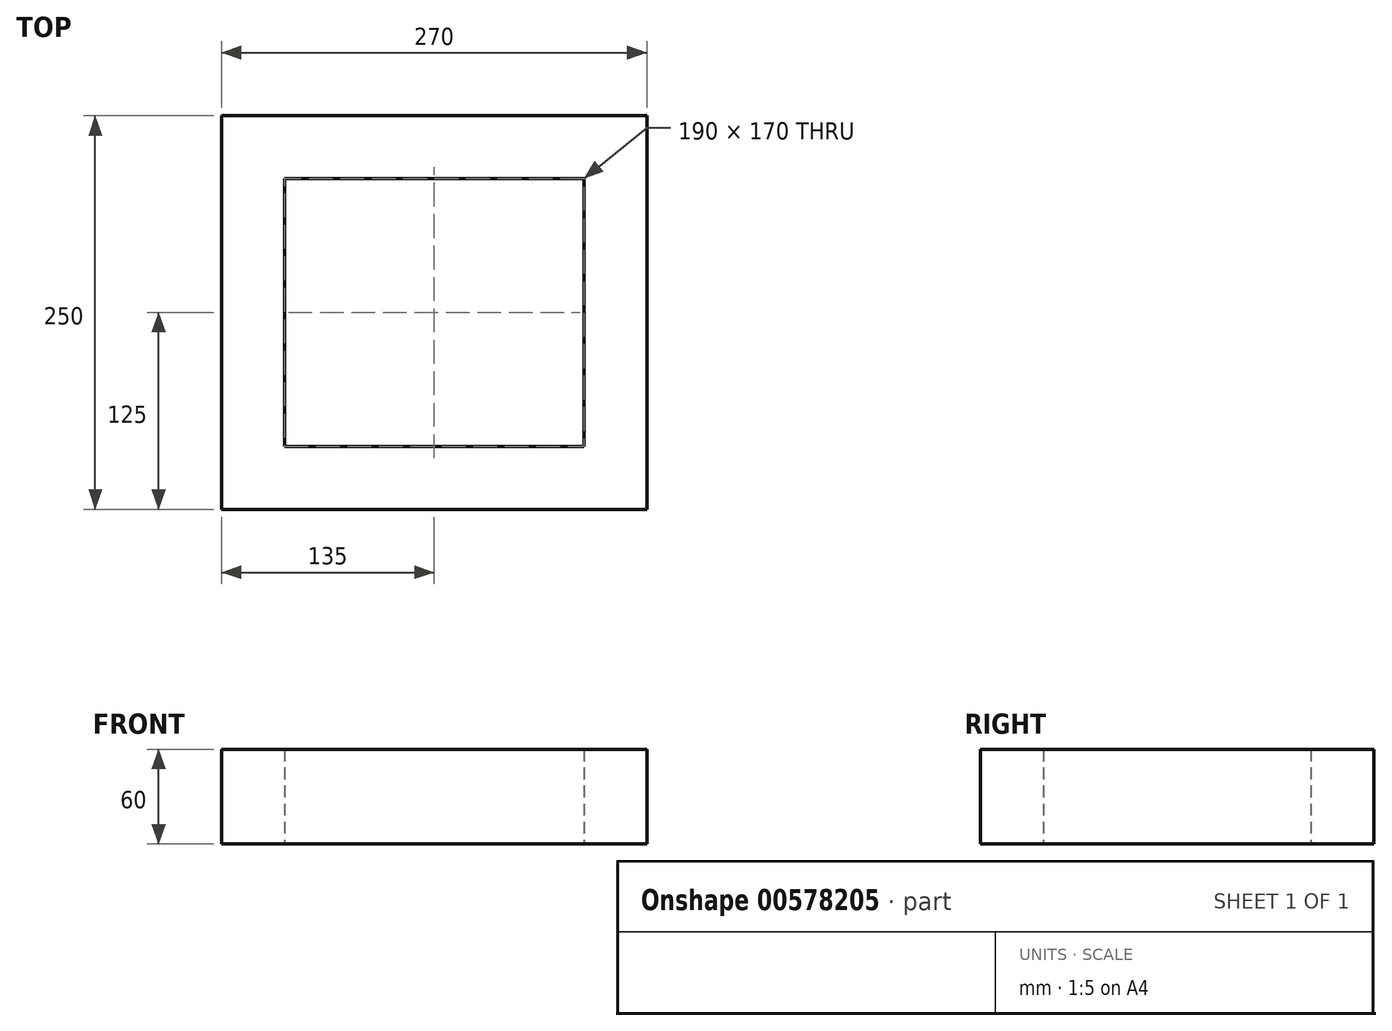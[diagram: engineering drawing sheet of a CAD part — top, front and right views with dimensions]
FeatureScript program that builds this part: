
annotation { "Feature Type Name" : "Feature", "Feature Type Description" : "" }
export const myFeature = defineFeature(function(context is Context, id is Id, definition is map)
    precondition{}
    {
        {
            var Q0;
            Q0=qCreatedBy(makeId("Top.planeOp"),FACE);
            var sketch = newSketch(context, id + "F0", { "sketchPlane" : qUnion([Q0])});
            skLineSegment(sketch, "E0.bottom", {"start": v(95, -85) * mm, "end": v(-95, -85) * mm});
            skLineSegment(sketch, "E0.top", {"start": v(95, 85) * mm, "end": v(-95, 85) * mm});
            skLineSegment(sketch, "E0.left", {"start": v(95, -85) * mm, "end": v(95, 85) * mm});
            skLineSegment(sketch, "E0.right", {"start": v(-95, -85) * mm, "end": v(-95, 85) * mm});
            skPoint(sketch, "E0.middle", {"position": v(0, 0) * mm});
            skLineSegment(sketch, "E1.bottom", {"start": v(135, -125) * mm, "end": v(-135, -125) * mm});
            skLineSegment(sketch, "E1.top", {"start": v(135, 125) * mm, "end": v(-135, 125) * mm});
            skLineSegment(sketch, "E1.left", {"start": v(135, -125) * mm, "end": v(135, 125) * mm});
            skLineSegment(sketch, "E1.right", {"start": v(-135, -125) * mm, "end": v(-135, 125) * mm});
            skSolve(sketch);
        }
        {
            var Q0;
            Q0 = qSketchRegion(id + "F0", true);
            extrude(context, id + "F1", {"entities" : qUnion([Q0]), "depth" : 60 * mm, "offsetDistance" : 25 * mm});
        }
    });
